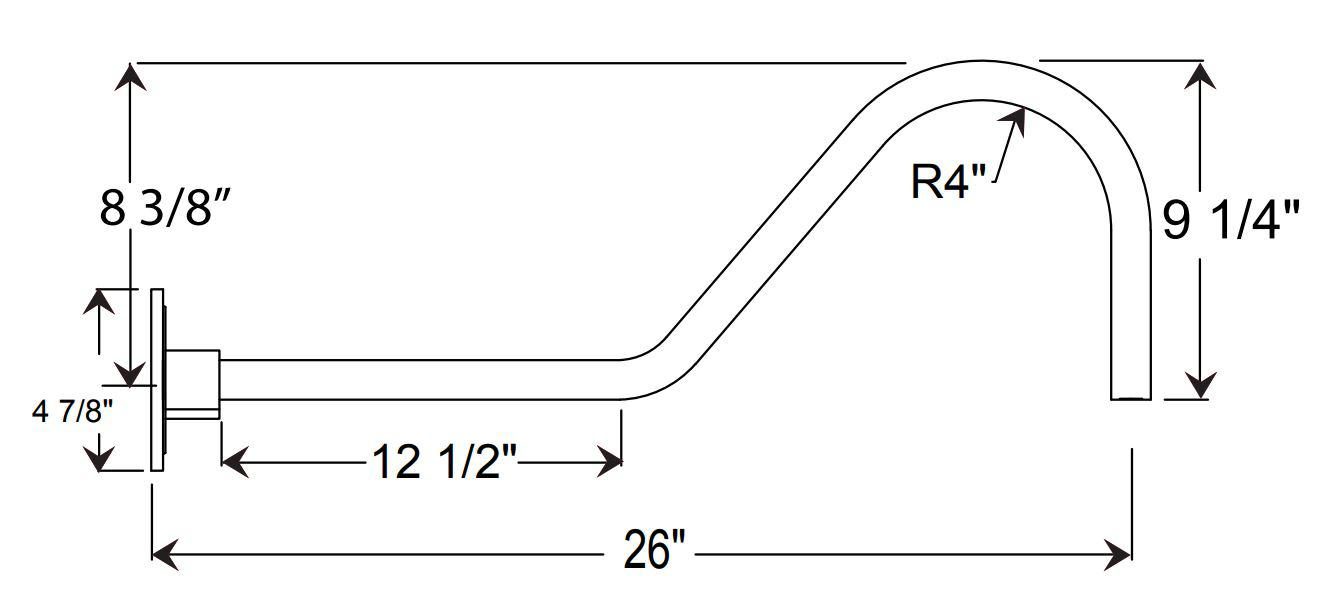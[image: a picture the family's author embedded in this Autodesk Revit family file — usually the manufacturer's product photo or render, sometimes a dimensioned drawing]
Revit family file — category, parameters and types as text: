
# Revit family: OSNC MB 24,36,40
name_source: partatom
category: Lighting Fixtures
units: mm (PartAtom-declared; Revit-internal decimal feet)

## family parameters
Always vertical = Yes
Cut with Voids When Loaded = No
Light Source = Yes
OmniClass Number = 23.80.70.00
OmniClass Title = Lighting
Part Type = Normal
Room Calculation Point = No
Round Connector Dimension = Use Diameter
Shared = No
Work Plane-Based = No

## types (3) — shared parameters
Apparent Load = 200 VA
Body Colour = Spun aluminium
Body Material = body
Bulb = Glass
CRI = >90
Canopy Body = Texture Black
Color Filter = 16777215
Construction Material = Heavy Duty spun aluminum.
Default Elevation = 0' - 0"
Description = 120-277 Voltage
Dimming = 1%
Dimming Lamp Color Temperature Shift = <None>
Efficiency = 65-125 lumens per watt
INSIDE BODY = white
Lamp = MB
Life = L70 50,000 hours
Load Classification = Lighting
Manufacturer = ANP Lighting
Photometric Web File = generic
Power Factor = 1
Tilt Angle = 90.00°
URL = https://www.anplighting.com
Voltage = 120 V
Warranty = 5 year limited warranty
Wattage Comments = 200 W

## per-type parameters (varying)
| type | Fixture Diameter | Fixture Height | OSNC24 | OSNC36 | OSNC40 | Weight | a | b |
| OSNC24 | 2' - 0" | 1' - 6" | Yes | No | No | 10.0 lbs | 1' - 6" | 0' - 2" |
| OSNC36 | 3' - 0" | 2' - 3" | No | Yes | No | 22.5 lbs | 2' - 3" | 0' - 5" |
| OSNC40 | 3' - 4" | 2' - 6" | No | No | Yes | 24.0 lbs | 2' - 6" | 0' - 5" |

note: column(s) folded — value = type name in every type: Model

## geometry (parser evidence)
native form markers: Sweep x36
no freeform markers — native parametric forms only
